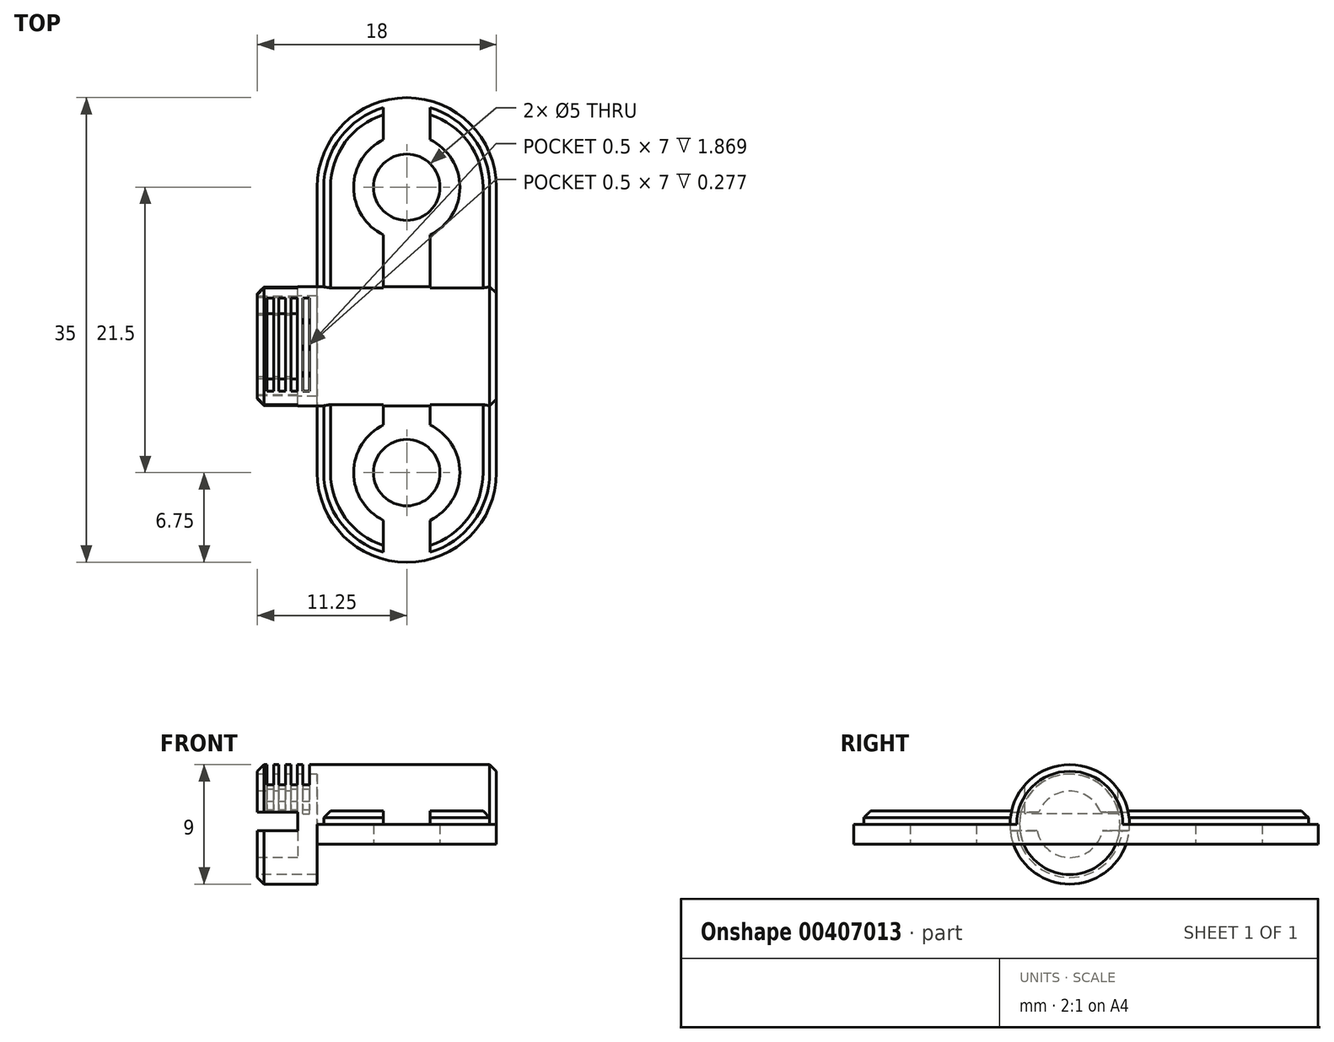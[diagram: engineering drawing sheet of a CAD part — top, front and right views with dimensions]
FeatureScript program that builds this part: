
annotation { "Feature Type Name" : "Feature", "Feature Type Description" : "" }
export const myFeature = defineFeature(function(context is Context, id is Id, definition is map)
    precondition{}
    {
        {
            var Q0;
            Q0=qCreatedBy(makeId("Top.planeOp"),FACE);
            var sketch = newSketch(context, id + "F0", { "sketchPlane" : qUnion([Q0])});
            skArc(sketch, "E0", {"start": v(6.75, 0) * mm, "mid": v(0, 6.75) * mm, "end": v(-6.75, 0) * mm});
            skArc(sketch, "E1", {"start": v(-6.75, -21.5) * mm, "mid": v(0, -28.25) * mm, "end": v(6.75, -21.5) * mm});
            skLineSegment(sketch, "E2", {"start": v(6.75, 0) * mm, "end": v(6.75, -21.5) * mm});
            skLineSegment(sketch, "E3", {"start": v(-6.75, 0) * mm, "end": v(-6.75, -21.5) * mm});
            skSolve(sketch);
        }
        {
            var Q0;
            Q0=qCreatedBy(makeId("Top.planeOp"),FACE);
            cPlane(context, id + "F1", {"entities" : qUnion([Q0]), "cplaneType" : CPlaneType.OFFSET, "offset" : 1.5 * mm, "width" : 150 * mm, "height" : 150 * mm});
        }
        {
            var Q0;
            Q0=qCreatedBy(id+"F1.planeOp",FACE);
            var sketch = newSketch(context, id + "F2", { "sketchPlane" : qUnion([Q0])});
            skLineSegment(sketch, "E4.0.0", {"start": v(-6.75, 0) * mm, "end": v(-6.75, -21.5) * mm});
            skArc(sketch, "E4.0.1", {"start": v(-6.75, -21.5) * mm, "mid": v(0, -28.25) * mm, "end": v(6.75, -21.5) * mm});
            skLineSegment(sketch, "E4.0.2", {"start": v(6.75, -21.5) * mm, "end": v(6.75, 0) * mm});
            skArc(sketch, "E4.0.3", {"start": v(6.75, 0) * mm, "mid": v(0, 6.75) * mm, "end": v(-6.75, 0) * mm});
            skArc(sketch, "E5.0", {"start": v(6.25, 0) * mm, "mid": v(0, 6.25) * mm, "end": v(-6.25, 0) * mm});
            skLineSegment(sketch, "E5.1", {"start": v(6.25, -21.5) * mm, "end": v(6.25, 0) * mm});
            skArc(sketch, "E5.2", {"start": v(-6.25, -21.5) * mm, "mid": v(0, -27.75) * mm, "end": v(6.25, -21.5) * mm});
            skLineSegment(sketch, "E5.3", {"start": v(-6.25, 0) * mm, "end": v(-6.25, -21.5) * mm});
            skCircle(sketch, "E6", {"center": v(0, 0) * mm, "radius": 3 * mm});
            skCircle(sketch, "E7", {"center": v(0, -21.5) * mm, "radius": 3 * mm});
            skSolve(sketch);
        }
        {
            var Q0;
            Q0=makeQuery(id+"F0.imprint","IMPRINT",FACE,{"disambiguationData":[TD([[makeQuery(id+"F0.imprint","IMPRINT",EDGE,{"derivedFrom":sQuery(id+"F0.wireOp",EDGE,"E0")}),1.0]])]});
            extrude(context, id + "F3", {"entities" : qUnion([Q0]), "depth" : 1.5 * mm});
        }
        {
            var Q0;
            Q0=makeQuery(id+"F2.imprint","IMPRINT",FACE,{"disambiguationData":[TD([[makeQuery(id+"F2.imprint","IMPRINT",EDGE,{"derivedFrom":sQuery(id+"F2.wireOp",EDGE,"E5.0")}),1.0]])]});
            var Q1;
            Q1=makeQuery(id+"F2.imprint","IMPRINT",FACE,{"disambiguationData":[TD([[makeQuery(id+"F2.imprint","IMPRINT",EDGE,{"derivedFrom":sQuery(id+"F2.wireOp",EDGE,"E6")}),1.0]])]});
            var Q2;
            Q2=makeQuery(id+"F2.imprint","IMPRINT",FACE,{"disambiguationData":[TD([[makeQuery(id+"F2.imprint","IMPRINT",EDGE,{"derivedFrom":sQuery(id+"F2.wireOp",EDGE,"E7")}),1.0]])]});
            extrude(context, id + "F4", {"entities" : qUnion([Q0, Q1, Q2]), "operationType" : NewBodyOperationType.ADD, "depth" : 1 * mm});
        }
        {
            var Q0;
            Q0=makeQuery(id+"F4.opExtrude","CAP_FACE",FACE,{"disambiguationData":[OSD([sQuery(id+"F2.wireOp",EDGE,"E5.0"),sQuery(id+"F2.wireOp",EDGE,"E5.1"),sQuery(id+"F2.wireOp",EDGE,"E5.2"),sQuery(id+"F2.wireOp",EDGE,"E5.3")])],"isStart":false});
            var sketch = newSketch(context, id + "F5", { "sketchPlane" : qUnion([Q0])});
            skCircle(sketch, "E8.0", {"center": v(0, 0) * mm, "radius": 3 * mm});
            skCircle(sketch, "E8.1", {"center": v(0, -21.5) * mm, "radius": 3 * mm});
            skSolve(sketch);
        }
        {
            var Q0;
            Q0=sQuery(id+"F5.wireOp",VERTEX,"E8.0.center");
            var Q1;
            Q1=sQuery(id+"F5.wireOp",VERTEX,"E8.1.center");
            var Q2;
            Q2=makeQuery(id+"F3.opExtrude","SWEPT_BODY",BODY,{"disambiguationData":[OSD([sQuery(id+"F0.wireOp",EDGE,"E0"),sQuery(id+"F0.wireOp",EDGE,"E1"),sQuery(id+"F0.wireOp",EDGE,"E2"),sQuery(id+"F0.wireOp",EDGE,"E3")])]});
            hole(context, id + "F6", {"style" : HoleStyle.C_BORE, "endStyle" : HoleEndStyle.BLIND, "holeDiameter" : 5 * mm, "cBoreDiameter" : 8 * mm, "cBoreDepth" : 1 * mm, "holeDepth" : 4 * mm, "isTappedThrough" : true, "tappedDepth" : 12 * mm, "tapClearance" : 3, "locations" : qUnion([Q0, Q1]), "scope" : qUnion([Q2]), "startStyle" : HoleStartStyle.SKETCH});
        }
        {
            var Q0;
            Q0=makeQuery(id+"F5.imprint","IMPRINT",FACE,{"disambiguationData":[TD([[makeQuery(id+"F5.imprint","IMPRINT",EDGE,{"derivedFrom":sQuery(id+"F5.wireOp",EDGE,"E8.0")}),-1.0]])]});
            var sketch = newSketch(context, id + "F7", { "sketchPlane" : qUnion([Q0])});
            skLineSegment(sketch, "E9.bottom", {"start": v(1.75, 8.89) * mm, "end": v(-1.75, 8.89) * mm});
            skLineSegment(sketch, "E9.top", {"start": v(1.75, -35.08) * mm, "end": v(-1.75, -35.08) * mm});
            skLineSegment(sketch, "E9.left", {"start": v(1.75, 8.89) * mm, "end": v(1.75, -35.08) * mm});
            skLineSegment(sketch, "E9.right", {"start": v(-1.75, 8.89) * mm, "end": v(-1.75, -35.08) * mm});
            skPoint(sketch, "E9.middle", {"position": v(0, -13.1) * mm});
            skSolve(sketch);
        }
        {
            var Q0;
            Q0 = qSketchRegion(id + "F7", true);
            var Q1;
            Q1=makeQuery(id+"F3.opExtrude","CAP_FACE",FACE,{"disambiguationData":[OSD([sQuery(id+"F0.wireOp",EDGE,"E0"),sQuery(id+"F0.wireOp",EDGE,"E1"),sQuery(id+"F0.wireOp",EDGE,"E2"),sQuery(id+"F0.wireOp",EDGE,"E3")])],"isStart":false});
            extrude(context, id + "F8", {"entities" : qUnion([Q0]), "operationType" : NewBodyOperationType.REMOVE, "endBound" : BoundingType.UP_TO_SURFACE, "oppositeDirection" : true, "endBoundEntityFace" : qUnion([Q1]), "depth" : 25 * mm});
        }
        {
            var Q0;
            Q0=makeQuery(id+"F3.opExtrude","SWEPT_FACE",FACE,{"disambiguationData":[OSD([sQuery(id+"F0.wireOp",EDGE,"E2")])]});
            var sketch = newSketch(context, id + "F9", { "sketchPlane" : qUnion([Q0])});
            skCircle(sketch, "E10", {"center": v(-11.98, 1.5) * mm, "radius": 4.5 * mm});
            skLineSegment(sketch, "E11", {"start": v(-16.22, 0) * mm, "end": v(-7.74, 0) * mm});
            skSolve(sketch);
        }
        {
            var Q0;
            Q0 = qSketchRegion(id + "F9", true);
            extrude(context, id + "F10", {"entities" : qUnion([Q0]), "oppositeDirection" : true, "depth" : 18 * mm});
        }
        {
            var Q0;
            {var subQ0=sQuery(id+"F9.wireOp",EDGE,"E11");Q0=makeQuery(id+"F9.imprint","IMPRINT",FACE,{"disambiguationData":[TD([[makeQuery(id+"F9.imprint","IMPRINT",EDGE,{"derivedFrom":subQ0}),1.0]])]});}
            var Q1;
            Q1=makeQuery(id+"F3.opExtrude","SWEPT_FACE",FACE,{"disambiguationData":[OSD([sQuery(id+"F0.wireOp",EDGE,"E3")])]});
            extrude(context, id + "F11", {"entities" : qUnion([Q0]), "operationType" : NewBodyOperationType.REMOVE, "endBound" : BoundingType.UP_TO_SURFACE, "oppositeDirection" : true, "endBoundEntityFace" : qUnion([Q1]), "depth" : 25 * mm});
        }
        {
            var Q0;
            Q0=makeQuery(id+"F10.opExtrude","CAP_FACE",FACE,{"disambiguationData":[OSD([sQuery(id+"F9.wireOp",EDGE,"E10")])],"isStart":false});
            var sketch = newSketch(context, id + "F12", { "sketchPlane" : qUnion([Q0])});
            skCircle(sketch, "E12", {"center": v(11.98, 1.5) * mm, "radius": 3.78 * mm});
            skSolve(sketch);
        }
        {
            var Q0;
            Q0 = qSketchRegion(id + "F12", true);
            var Q1;
            Q1=makeQuery(id+"F3.opExtrude","SWEPT_FACE",FACE,{"disambiguationData":[OSD([sQuery(id+"F0.wireOp",EDGE,"E3")])]});
            extrude(context, id + "F13", {"entities" : qUnion([Q0]), "endBound" : BoundingType.UP_TO_SURFACE, "oppositeDirection" : true, "endBoundEntityFace" : qUnion([Q1]), "depth" : 25 * mm});
        }
        {
            var Q0;
            Q0=makeQuery(id+"F5.imprint","IMPRINT",FACE,{"disambiguationData":[TD([[makeQuery(id+"F5.imprint","IMPRINT",EDGE,{"derivedFrom":sQuery(id+"F5.wireOp",EDGE,"E8.0")}),-1.0]])]});
            cPlane(context, id + "F14", {"entities" : qUnion([Q0]), "cplaneType" : CPlaneType.OFFSET, "offset" : 4.5 * mm, "width" : 150 * mm, "height" : 150 * mm});
        }
        {
            var Q0;
            Q0=qCreatedBy(id+"F14.planeOp",FACE);
            var sketch = newSketch(context, id + "F15", { "sketchPlane" : qUnion([Q0])});
            skLineSegment(sketch, "E13.bottom", {"start": v(-10.53, -8.36) * mm, "end": v(-10.03, -8.36) * mm});
            skLineSegment(sketch, "E13.top", {"start": v(-10.53, -15.36) * mm, "end": v(-10.03, -15.36) * mm});
            skLineSegment(sketch, "E13.left", {"start": v(-10.03, -8.36) * mm, "end": v(-10.03, -15.36) * mm});
            skLineSegment(sketch, "E13.right", {"start": v(-10.53, -8.36) * mm, "end": v(-10.53, -15.36) * mm});
            skLineSegment(sketch, "E14.1.0.0", {"start": v(-9.13, -8.36) * mm, "end": v(-9.13, -15.36) * mm});
            skLineSegment(sketch, "E14.1.0.1", {"start": v(-9.63, -8.36) * mm, "end": v(-9.63, -15.36) * mm});
            skLineSegment(sketch, "E14.1.0.2", {"start": v(-9.63, -15.36) * mm, "end": v(-9.13, -15.36) * mm});
            skLineSegment(sketch, "E14.1.0.3", {"start": v(-9.63, -8.36) * mm, "end": v(-9.13, -8.36) * mm});
            skLineSegment(sketch, "E14.2.0.0", {"start": v(-8.23, -8.36) * mm, "end": v(-8.23, -15.36) * mm});
            skLineSegment(sketch, "E14.2.0.1", {"start": v(-8.73, -8.36) * mm, "end": v(-8.73, -15.36) * mm});
            skLineSegment(sketch, "E14.2.0.2", {"start": v(-8.73, -15.36) * mm, "end": v(-8.23, -15.36) * mm});
            skLineSegment(sketch, "E14.2.0.3", {"start": v(-8.73, -8.36) * mm, "end": v(-8.23, -8.36) * mm});
            skLineSegment(sketch, "E14.3.0.0", {"start": v(-7.33, -8.36) * mm, "end": v(-7.33, -15.36) * mm});
            skLineSegment(sketch, "E14.3.0.1", {"start": v(-7.83, -8.36) * mm, "end": v(-7.83, -15.36) * mm});
            skLineSegment(sketch, "E14.3.0.2", {"start": v(-7.83, -15.36) * mm, "end": v(-7.33, -15.36) * mm});
            skLineSegment(sketch, "E14.3.0.3", {"start": v(-7.83, -8.36) * mm, "end": v(-7.33, -8.36) * mm});
            skLineSegment(sketch, "E14.direction1", {"start": v(-10.03, -15.36) * mm, "end": v(-9.13, -15.36) * mm, "construction": true});
            skSolve(sketch);
        }
        {
            var Q0;
            Q0=makeQuery(id+"F15.imprint","IMPRINT",FACE,{"disambiguationData":[TD([[makeQuery(id+"F15.imprint","IMPRINT",EDGE,{"derivedFrom":sQuery(id+"F15.wireOp",EDGE,"E13.bottom")}),-1.0]])]});
            var Q1;
            Q1=makeQuery(id+"F15.imprint","IMPRINT",FACE,{"disambiguationData":[TD([[makeQuery(id+"F15.imprint","IMPRINT",EDGE,{"derivedFrom":sQuery(id+"F15.wireOp",EDGE,"E14.1.0.0")}),-1.0]])]});
            var Q2;
            Q2=makeQuery(id+"F15.imprint","IMPRINT",FACE,{"disambiguationData":[TD([[makeQuery(id+"F15.imprint","IMPRINT",EDGE,{"derivedFrom":sQuery(id+"F15.wireOp",EDGE,"E14.2.0.0")}),-1.0]])]});
            var Q3;
            Q3=makeQuery(id+"F15.imprint","IMPRINT",FACE,{"disambiguationData":[TD([[makeQuery(id+"F15.imprint","IMPRINT",EDGE,{"derivedFrom":sQuery(id+"F15.wireOp",EDGE,"E14.3.0.0")}),-1.0]])]});
            extrude(context, id + "F16", {"entities" : qUnion([Q0, Q1, Q2, Q3]), "operationType" : NewBodyOperationType.REMOVE, "oppositeDirection" : true, "depth" : 4.7 * mm});
        }
        {
            var Q0;
            Q0=makeQuery(id+"F10.opExtrude","CAP_FACE",FACE,{"disambiguationData":[OSD([sQuery(id+"F9.wireOp",EDGE,"E10")])],"isStart":false});
            var sketch = newSketch(context, id + "F17", { "sketchPlane" : qUnion([Q0])});
            skCircle(sketch, "E15", {"center": v(11.98, 1.5) * mm, "radius": 2.5 * mm});
            skSolve(sketch);
        }
        {
            var Q0;
            Q0 = qSketchRegion(id + "F17", true);
            extrude(context, id + "F18", {"entities" : qUnion([Q0]), "operationType" : NewBodyOperationType.REMOVE, "oppositeDirection" : true, "depth" : 3.05 * mm});
        }
        {
            var Q0;
            Q0=makeQuery(id+"F10.opExtrude","CAP_FACE",FACE,{"disambiguationData":[OSD([sQuery(id+"F9.wireOp",EDGE,"E10")])],"isStart":false});
            var sketch = newSketch(context, id + "F19", { "sketchPlane" : qUnion([Q0])});
            skLineSegment(sketch, "E16.bottom", {"start": v(6.63, 2.43) * mm, "end": v(17.18, 2.43) * mm});
            skLineSegment(sketch, "E16.top", {"start": v(6.63, 1) * mm, "end": v(17.18, 1) * mm});
            skLineSegment(sketch, "E16.left", {"start": v(6.63, 2.43) * mm, "end": v(6.63, 1) * mm});
            skLineSegment(sketch, "E16.right", {"start": v(17.18, 2.43) * mm, "end": v(17.18, 1) * mm});
            skSolve(sketch);
        }
        {
            var Q0;
            Q0 = qSketchRegion(id + "F19", true);
            var Q1;
            Q1=makeQuery(id+"F18.boolean.opBoolean","COPY",FACE,{"derivedFrom":makeQuery(id+"F18.opExtrude","CAP_FACE",FACE,{"disambiguationData":[OSD([sQuery(id+"F17.wireOp",EDGE,"E15")])],"isStart":false})});
            extrude(context, id + "F20", {"entities" : qUnion([Q0]), "operationType" : NewBodyOperationType.REMOVE, "endBound" : BoundingType.UP_TO_SURFACE, "oppositeDirection" : true, "endBoundEntityFace" : qUnion([Q1]), "depth" : 25 * mm});
        }
        {
            var Q0;
            Q0=makeQuery(id+"F3.opExtrude","SWEPT_BODY",BODY,{"disambiguationData":[OSD([sQuery(id+"F0.wireOp",EDGE,"E0"),sQuery(id+"F0.wireOp",EDGE,"E1"),sQuery(id+"F0.wireOp",EDGE,"E2"),sQuery(id+"F0.wireOp",EDGE,"E3")])]});
            var Q1;
            Q1=makeQuery(id+"F10.opExtrude","SWEPT_BODY",BODY,{"disambiguationData":[OSD([sQuery(id+"F9.wireOp",EDGE,"E10")])]});
            booleanBodies(context, id + "F21", {"operationType" : BooleanOperationType.UNION, "tools" : qUnion([Q0, Q1])});
        }
        {
            var Q0;
            {var subQ0=sQuery(id+"F9.wireOp",EDGE,"E10");Q0=makeQuery(id+"F20.boolean.opBoolean","SPLIT",EDGE,{"disambiguationData":[TD([makeQuery(id+"F20.opExtrude","SWEPT_FACE",FACE,{"disambiguationData":[OSD([sQuery(id+"F19.wireOp",EDGE,"E16.bottom")])]})])],"derivedFrom":makeQuery(id+"F10.opExtrude","CAP_EDGE",EDGE,{"disambiguationData":[OSD([subQ0])],"isStart":false})});}
            var Q1;
            {var subQ0=sQuery(id+"F9.wireOp",EDGE,"E10");Q1=makeQuery(id+"F20.boolean.opBoolean","SPLIT",EDGE,{"disambiguationData":[TD([makeQuery(id+"F20.opExtrude","SWEPT_FACE",FACE,{"disambiguationData":[OSD([sQuery(id+"F19.wireOp",EDGE,"E16.top")])]})])],"derivedFrom":makeQuery(id+"F10.opExtrude","CAP_EDGE",EDGE,{"disambiguationData":[OSD([subQ0])],"isStart":false})});}
            var Q2;
            Q2=makeQuery(id+"F10.opExtrude","CAP_EDGE",EDGE,{"disambiguationData":[OSD([sQuery(id+"F9.wireOp",EDGE,"E10")])],"isStart":true});
            var Q3;
            {var subQ0=sQuery(id+"F2.wireOp",EDGE,"E5.0");var subQ1=sQuery(id+"F2.wireOp",EDGE,"E5.1");Q3=makeQuery(id+"F21.opBoolean","SPLIT",EDGE,{"disambiguationData":[TD([makeQuery(id+"F4.opExtrude","SWEPT_FACE",FACE,{"disambiguationData":[OSD([subQ0])]})])],"derivedFrom":makeQuery(id+"F4.opExtrude","CAP_EDGE",EDGE,{"disambiguationData":[OSD([subQ1])],"isStart":false})});}
            var Q4;
            {var subQ0=sQuery(id+"F2.wireOp",EDGE,"E5.0");var subQ1=sQuery(id+"F2.wireOp",EDGE,"E5.3");Q4=makeQuery(id+"F8.boolean.opBoolean","SPLIT",EDGE,{"disambiguationData":[TD([makeQuery(id+"F4.opExtrude","SWEPT_FACE",FACE,{"disambiguationData":[OSD([subQ1])]})])],"derivedFrom":makeQuery(id+"F4.opExtrude","CAP_EDGE",EDGE,{"disambiguationData":[OSD([subQ0])],"isStart":false})});}
            var Q5;
            {var subQ0=sQuery(id+"F2.wireOp",EDGE,"E5.2");var subQ1=sQuery(id+"F2.wireOp",EDGE,"E5.1");Q5=makeQuery(id+"F21.opBoolean","SPLIT",EDGE,{"disambiguationData":[TD([makeQuery(id+"F4.opExtrude","SWEPT_FACE",FACE,{"disambiguationData":[OSD([subQ0])]})])],"derivedFrom":makeQuery(id+"F4.opExtrude","CAP_EDGE",EDGE,{"disambiguationData":[OSD([subQ1])],"isStart":false})});}
            var Q6;
            {var subQ0=sQuery(id+"F2.wireOp",EDGE,"E5.3");var subQ1=sQuery(id+"F2.wireOp",EDGE,"E5.2");Q6=makeQuery(id+"F8.boolean.opBoolean","SPLIT",EDGE,{"disambiguationData":[TD([makeQuery(id+"F4.opExtrude","SWEPT_FACE",FACE,{"disambiguationData":[OSD([subQ0])]})])],"derivedFrom":makeQuery(id+"F4.opExtrude","CAP_EDGE",EDGE,{"disambiguationData":[OSD([subQ1])],"isStart":false})});}
            chamfer(context, id + "F22", {"entities" : qUnion([Q0, Q1, Q2, Q3, Q4, Q5, Q6]), "width" : 0.5 * mm, "tangentPropagation" : true});
        }
    });
